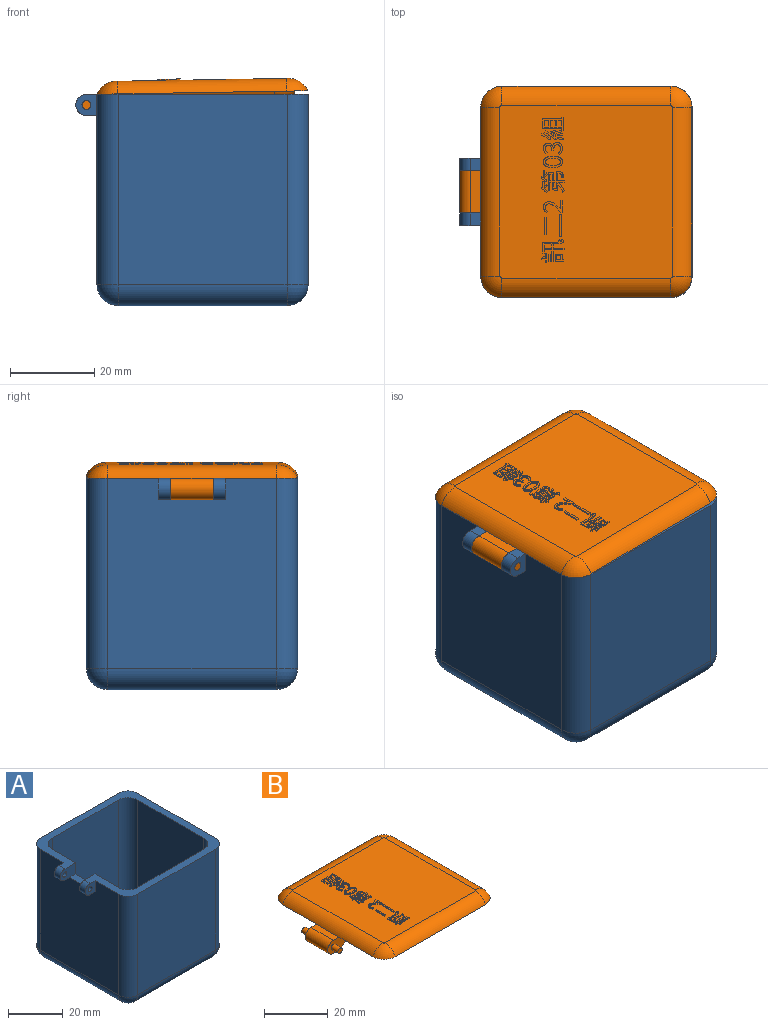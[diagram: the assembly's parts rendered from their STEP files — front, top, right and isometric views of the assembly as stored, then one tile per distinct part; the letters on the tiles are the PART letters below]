
ASSEMBLY  parts=2 mates=1
PART A: 46 faces, bbox 55x50x50 mm
  f0: plane 8x5mm, normal (0,1,0), area 33.9mm2, adj f3,f5,f13,f16,f19,f20
  f1: plane 8x5mm, normal (0,-1,0), area 33.9mm2, adj f3,f4,f13,f16,f18,f21
  f2: plane 5x5mm, normal (0,1,0), area 18.9mm2, adj f3,f4,f6,f18,f21
  f3: plane 52.5x50mm, normal (0,0,1), area 549mm2, adj f0,f1,f2,f6,f7,f8,f9,f11
  f4: plane 3x2.5mm, normal (0,0,-1), area 7.5mm2, adj f1,f2,f6,f18
  f5: plane 3x2.5mm, normal (0,0,-1), area 7.5mm2, adj f0,f6,f17,f19
  f6: plane 45x40mm, normal (-1,0,0), area 1720mm2, adj f2,f3,f4,f5,f16,f17,f34,f36
  f7: plane 45x40mm, normal (1,0,0), area 1800mm2, adj f3,f39,f43,f45
  f8: plane 45x40mm, normal (0,1,0), area 1800mm2, adj f3,f36,f42,f45
  f9: plane 45x40mm, normal (0,-1,0), area 1800mm2, adj f3,f34,f38,f39
  f10: plane 40x40mm, normal (0,0,-1), area 1600mm2, adj f37,f38,f42,f43
  f11: plane 42x34mm, normal (-1,0,0), area 1428mm2, adj f3,f22,f26,f27
  f12: plane 42x34mm, normal (0,-1,0), area 1428mm2, adj f3,f22,f24,f25
  f13: plane 42x34mm, normal (1,0,0), area 1378mm2, adj f0,f1,f3,f16,f24,f30,f33
  f14: plane 42x34mm, normal (0,1,0), area 1428mm2, adj f3,f27,f31,f33
  f15: plane 34x34mm, normal (0,0,1), area 1156mm2, adj f25,f26,f30,f31
  f16: plane 10x3mm, normal (0,0,1), area 30mm2, adj f0,f1,f6,f13
  f17: plane 5x5mm, normal (0,-1,0), area 18.9mm2, adj f3,f5,f6,f19,f20
  f18: cylinder r=2.5mm len=5mm, axis (0,-1,0), area 23.6mm2, adj f1,f2,f3,f4
  f19: cylinder r=2.5mm len=5mm, axis (0,-1,0), area 23.6mm2, adj f0,f3,f5,f17
  f20: cylinder r=1.05mm len=3mm, axis (0,-1,0), area 19.8mm2, adj f0,f17
  f21: cylinder r=1.05mm len=3mm, axis (0,-1,0), area 19.8mm2, adj f1,f2
  f22: cylinder r=5mm len=42mm, axis (0,0,-1), area 329.9mm2, adj f3,f11,f12,f23
  f23: sphere r=5mm, area 39.3mm2, adj f22,f25,f26
  f24: cylinder r=5mm len=42mm, axis (0,0,1), area 329.9mm2, adj f3,f12,f13,f28
  f25: cylinder r=5mm len=34mm, axis (1,0,0), area 267mm2, adj f12,f15,f23,f28
  f26: cylinder r=5mm len=34mm, axis (0,-1,0), area 267mm2, adj f11,f15,f23,f29
  f27: cylinder r=5mm len=42mm, axis (0,0,1), area 329.9mm2, adj f3,f11,f14,f29
  f28: sphere r=5mm, area 39.3mm2, adj f24,f25,f30
  f29: sphere r=5mm, area 39.3mm2, adj f26,f27,f31
  f30: cylinder r=5mm len=34mm, axis (0,1,0), area 267mm2, adj f13,f15,f28,f32
  f31: cylinder r=5mm len=34mm, axis (-1,0,0), area 267mm2, adj f14,f15,f29,f32
  f32: sphere r=5mm, area 39.3mm2, adj f30,f31,f33
  f33: cylinder r=5mm len=42mm, axis (0,0,-1), area 329.9mm2, adj f3,f13,f14,f32
  f34: cylinder r=5mm len=45mm, axis (0,0,1), area 353.4mm2, adj f3,f6,f9,f35
  f35: sphere r=5mm, area 39.3mm2, adj f34,f37,f38
  f36: cylinder r=5mm len=45mm, axis (0,0,-1), area 353.4mm2, adj f3,f6,f8,f40
  f37: cylinder r=5mm len=40mm, axis (0,-1,0), area 314.2mm2, adj f6,f10,f35,f40
  f38: cylinder r=5mm len=40mm, axis (1,0,0), area 314.2mm2, adj f9,f10,f35,f41
  f39: cylinder r=5mm len=45mm, axis (0,0,-1), area 353.4mm2, adj f3,f7,f9,f41
  f40: sphere r=5mm, area 39.3mm2, adj f36,f37,f42
  f41: sphere r=5mm, area 39.3mm2, adj f38,f39,f43
  f42: cylinder r=5mm len=40mm, axis (-1,0,0), area 314.2mm2, adj f8,f10,f40,f44
  f43: cylinder r=5mm len=40mm, axis (0,1,0), area 314.2mm2, adj f7,f10,f41,f44
  f44: sphere r=5mm, area 39.3mm2, adj f42,f43,f45
  f45: cylinder r=5mm len=45mm, axis (0,0,1), area 353.4mm2, adj f3,f7,f8,f44
PART B: 258 faces, bbox 55x50x8.3 mm
  f0: plane 40.84x40.84mm, normal (0,0,1), area 1603.1mm2, adj f12,f13,f14,f15,f17,f18,f19,f20
  f1: plane 12.58x5mm, normal (0,1,0), area 35.6mm2, adj f3,f4,f5,f6,f9,f11,f240,f249
  f2: plane 12.58x5mm, normal (0,-1,0), area 35.6mm2, adj f3,f4,f5,f6,f7,f11,f240,f241
  f3: plane 50x50mm, normal (0,0,-1), area 534mm2, adj f1,f2,f241,f242,f243,f244,f245,f246
  f4: plane 39.42x34.84mm, normal (0,0,-1), area 1259.1mm2, adj f1,f2,f240,f241,f242,f243,f244,f245
  f5: plane 10x1.5mm, normal (0,0,-1), area 15mm2, adj f1,f2,f11,f240
  f6: plane 10x2.5mm, normal (0,0,1), area 25mm2, adj f1,f2,f11,f252
  f7: cylinder r=1mm len=3mm, axis (0,1,0), area 18.8mm2, adj f2,f8
  f8: plane 2x2mm, normal (0,-1,0), area 3.1mm2, adj f7
  f9: cylinder r=1mm len=3mm, axis (0,-1,0), area 18.8mm2, adj f1,f10
  f10: plane 2x2mm, normal (0,1,0), area 3.1mm2, adj f9
  f11: cylinder r=2.5mm len=10mm, axis (0,-1,0), area 78.5mm2, adj f1,f2,f5,f6
  f12: plane 0.33x0.3mm, normal (0.85,0.53,0), area 0.1mm2, adj f0,f13,f15,f16
  f13: extruded ~0.76x0.43mm, area 0.3mm2, adj f0,f12,f14,f16
  f14: plane 0.31x0.3mm, normal (-0.87,-0.49,0), area 0.1mm2, adj f0,f13,f15,f16
  f15: extruded ~0.79x0.42mm, area 0.3mm2, adj f0,f12,f14,f16
  f16: plane 0.97x0.74mm, normal (0,0,1), area 0.3mm2, adj f12,f13,f14,f15
  f17: plane 0.36x0.3mm, normal (0,1,0), area 0.1mm2, adj f0,f18,f20,f21
  f18: plane 2.13x0.3mm, normal (-1,0,0), area 0.6mm2, adj f0,f17,f19,f21
  f19: plane 0.36x0.3mm, normal (0,-1,0), area 0.1mm2, adj f0,f18,f20,f21
  f20: plane 2.13x0.3mm, normal (1,0,0), area 0.6mm2, adj f0,f17,f19,f21
  f21: plane 2.13x0.36mm, normal (0,0,1), area 0.8mm2, adj f17,f18,f19,f20
  f22: plane 1.67x0.3mm, normal (1,0,0), area 0.5mm2, adj f0,f23,f25,f26
  f23: plane 0.35x0.3mm, normal (0,1,0), area 0.1mm2, adj f0,f22,f24,f26
  f24: plane 1.67x0.3mm, normal (-1,0,0), area 0.5mm2, adj f0,f23,f25,f26
  f25: plane 0.35x0.3mm, normal (0,-1,0), area 0.1mm2, adj f0,f22,f24,f26
  f26: plane 1.67x0.35mm, normal (0,0,1), area 0.6mm2, adj f22,f23,f24,f25
  f27: plane 0.96x0.3mm, normal (1,0,0), area 0.3mm2, adj f28,f36,f37,f38
  f28: plane 0.98x0.3mm, normal (0,-1,0), area 0.3mm2, adj f27,f29,f37,f38
  f29: plane 0.96x0.3mm, normal (-1,0,0), area 0.3mm2, adj f28,f36,f37,f38
  f30: plane 1.71x0.3mm, normal (0,1,0), area 0.5mm2, adj f0,f31,f35,f37
  f31: plane 1.68x0.3mm, normal (-1,0,0), area 0.5mm2, adj f0,f30,f32,f37
  f32: plane 1.99x0.3mm, normal (0,-1,0), area 0.6mm2, adj f0,f31,f33,f37
  f33: plane 0.36x0.3mm, normal (1,0,0), area 0.1mm2, adj f0,f32,f34,f37
  f34: plane 0.3x0.28mm, normal (0,1,0), area 0.1mm2, adj f0,f33,f35,f37
  f35: plane 1.32x0.3mm, normal (1,0,0), area 0.4mm2, adj f0,f30,f34,f37
  f36: plane 0.98x0.3mm, normal (0,1,0), area 0.3mm2, adj f27,f29,f37,f38
  f37: plane 1.99x1.68mm, normal (0,0,1), area 2mm2, adj f27,f28,f29,f30,f31,f32,f33,f34
  f38: plane 0.98x0.96mm, normal (0,0,1), area 0.9mm2, adj f27,f28,f29,f36
  f39: plane 0.35x0.3mm, normal (0,-1,0), area 0.1mm2, adj f0,f40,f42,f43
  f40: plane 1.68x0.3mm, normal (1,0,0), area 0.5mm2, adj f0,f39,f41,f43
  f41: plane 0.35x0.3mm, normal (0,1,0), area 0.1mm2, adj f0,f40,f42,f43
  f42: plane 1.68x0.3mm, normal (-1,0,0), area 0.5mm2, adj f0,f39,f41,f43
  f43: plane 1.68x0.35mm, normal (0,0,1), area 0.6mm2, adj f39,f40,f41,f42
  f44: plane 2.58x0.3mm, normal (-1,0,0), area 0.8mm2, adj f0,f45,f63,f64
  f45: plane 0.42x0.3mm, normal (0,-1,0), area 0.1mm2, adj f0,f44,f46,f64
  f46: plane 0.74x0.3mm, normal (1,0,0), area 0.2mm2, adj f0,f45,f47,f64
  f47: plane 1.75x0.3mm, normal (0,-1,0), area 0.5mm2, adj f0,f46,f48,f64
  f48: plane 0.8x0.3mm, normal (-1,0,0), area 0.2mm2, adj f0,f47,f49,f64
  f49: plane 0.41x0.3mm, normal (0,-1,0), area 0.1mm2, adj f0,f48,f50,f64
  f50: plane 0.8x0.3mm, normal (1,0,0), area 0.2mm2, adj f0,f49,f51,f64
  f51: plane 2.5x0.3mm, normal (0,-1,0), area 0.7mm2, adj f0,f50,f52,f64
  f52: plane 0.42x0.3mm, normal (1,0,0), area 0.1mm2, adj f0,f51,f53,f64
  f53: plane 2.5x0.3mm, normal (0,1,0), area 0.7mm2, adj f0,f52,f54,f64
  f54: plane 0.78x0.3mm, normal (1,0,0), area 0.2mm2, adj f0,f53,f55,f64
  f55: plane 0.41x0.3mm, normal (0,1,0), area 0.1mm2, adj f0,f54,f56,f64
  f56: plane 0.78x0.3mm, normal (-1,0,0), area 0.2mm2, adj f0,f55,f57,f64
  f57: plane 1.75x0.3mm, normal (0,1,0), area 0.5mm2, adj f0,f56,f58,f64
  f58: plane 0.98x0.3mm, normal (1,0,0), area 0.3mm2, adj f0,f57,f59,f64
  f59: extruded ~4.55x0.56mm, area 1.4mm2, adj f0,f58,f60,f64
  f60: extruded ~0.94x0.53mm, area 0.4mm2, adj f0,f59,f61,f64
  f61: extruded ~0.32x0.3mm, area 0.1mm2, adj f0,f60,f62,f64
  f62: extruded ~0.8x0.3mm, area 0.2mm2, adj f0,f61,f63,f64
  f63: extruded ~4.54x0.3mm, area 1.4mm2, adj f0,f44,f62,f64
  f64: plane 5.08x3.29mm, normal (0,0,1), area 5.9mm2, adj f44,f45,f46,f47,f48,f49,f50,f51
  f65: plane 4.23x0.3mm, normal (-1,0,0), area 1.3mm2, adj f0,f66,f68,f69
  f66: plane 0.47x0.3mm, normal (0,-1,0), area 0.1mm2, adj f0,f65,f67,f69
  f67: plane 4.23x0.3mm, normal (1,0,0), area 1.3mm2, adj f0,f66,f68,f69
  f68: plane 0.47x0.3mm, normal (0,1,0), area 0.1mm2, adj f0,f65,f67,f69
  f69: plane 4.23x0.47mm, normal (0,0,1), area 2mm2, adj f65,f66,f67,f68
  f70: plane 5.23x0.3mm, normal (-1,0,0), area 1.6mm2, adj f0,f71,f73,f74
  f71: plane 0.48x0.3mm, normal (0,-1,0), area 0.1mm2, adj f0,f70,f72,f74
  f72: plane 5.23x0.3mm, normal (1,0,0), area 1.6mm2, adj f0,f71,f73,f74
  f73: plane 0.48x0.3mm, normal (0,1,0), area 0.1mm2, adj f0,f70,f72,f74
  f74: plane 5.23x0.48mm, normal (0,0,1), area 2.5mm2, adj f70,f71,f72,f73
  f75: plane 0.32x0.3mm, normal (0,-1,0), area 0.1mm2, adj f0,f76,f86,f87
  f76: plane 2.73x0.3mm, normal (1,0,0), area 0.8mm2, adj f0,f75,f77,f87
  f77: plane 0.47x0.3mm, normal (0,1,0), area 0.1mm2, adj f0,f76,f78,f87
  f78: plane 1.2x0.3mm, normal (-1,0,0), area 0.4mm2, adj f0,f77,f79,f87
  f79: extruded ~0.71x0.3mm, area 0.2mm2, adj f0,f78,f80,f87
  f80: extruded ~2.72x1.7mm, area 1mm2, adj f0,f79,f81,f87
  f81: extruded ~1.29x1.26mm, area 0.6mm2, adj f0,f80,f82,f87
  f82: extruded ~1.28x0.64mm, area 0.4mm2, adj f0,f81,f83,f87
  f83: plane 0.31x0.31mm, normal (0.71,-0.7,0), area 0.1mm2, adj f0,f82,f84,f87
  f84: extruded ~0.9x0.5mm, area 0.3mm2, adj f0,f83,f85,f87
  f85: extruded ~0.86x0.8mm, area 0.4mm2, adj f0,f84,f86,f87
  f86: extruded ~2.81x1.99mm, area 1.1mm2, adj f0,f75,f85,f87
  f87: plane 4.43x2.76mm, normal (0,0,1), area 4.3mm2, adj f75,f76,f77,f78,f79,f80,f81,f82
  f88: plane 0.51x0.3mm, normal (1,0,0), area 0.2mm2, adj f0,f89,f100,f101
  f89: plane 0.3x0.23mm, normal (-0.8,-0.61,0), area 0.1mm2, adj f0,f88,f90,f101
  f90: extruded ~0.6x0.56mm, area 0.2mm2, adj f0,f89,f91,f101
  f91: plane 0.3x0.29mm, normal (0.77,0.64,0), area 0.1mm2, adj f0,f90,f92,f101
  f92: extruded ~0.53x0.53mm, area 0.2mm2, adj f0,f91,f93,f101
  f93: plane 1.12x0.3mm, normal (1,0,0), area 0.3mm2, adj f0,f92,f94,f101
  f94: plane 0.36x0.3mm, normal (0,1,0), area 0.1mm2, adj f0,f93,f95,f101
  f95: plane 1.52x0.3mm, normal (-1,0,0), area 0.5mm2, adj f0,f94,f96,f101
  f96: extruded ~0.36x0.3mm, area 0.1mm2, adj f0,f95,f97,f101
  f97: plane 0.39x0.3mm, normal (-0.96,0.27,0), area 0.1mm2, adj f0,f96,f98,f101
  f98: extruded ~1.29x0.9mm, area 0.5mm2, adj f0,f97,f99,f101
  f99: extruded ~0.31x0.3mm, area 0.1mm2, adj f0,f98,f100,f101
  f100: extruded ~0.77x0.61mm, area 0.3mm2, adj f0,f88,f99,f101
  f101: plane 2.64x1.6mm, normal (0,0,1), area 1.5mm2, adj f88,f89,f90,f91,f92,f93,f94,f95
  f102: plane 1.33x0.3mm, normal (1,0,0), area 0.4mm2, adj f103,f135,f136,f138
  f103: plane 0.55x0.3mm, normal (0,-1,0), area 0.2mm2, adj f102,f104,f136,f138
  f104: plane 1.42x0.3mm, normal (-1,0,0), area 0.4mm2, adj f103,f135,f136,f138
  f105: plane 0.55x0.3mm, normal (0,1,0), area 0.2mm2, adj f106,f133,f136,f137
  f106: plane 1.55x0.3mm, normal (1,0,0), area 0.5mm2, adj f105,f107,f136,f137
  f107: plane 0.55x0.3mm, normal (0,-1,0), area 0.2mm2, adj f106,f133,f136,f137
  f108: plane 2.18x0.3mm, normal (-1,0,0), area 0.7mm2, adj f0,f109,f134,f136
  f109: plane 0.55x0.3mm, normal (0,1,0), area 0.2mm2, adj f0,f108,f110,f136
  f110: plane 1.99x0.3mm, normal (1,0,0), area 0.6mm2, adj f0,f109,f111,f136
  f111: plane 1.29x0.3mm, normal (0,1,0), area 0.4mm2, adj f0,f110,f112,f136
  f112: plane 4.34x0.3mm, normal (-1,0,0), area 1.3mm2, adj f0,f111,f113,f136
  f113: plane 0.37x0.3mm, normal (0,-1,0), area 0.1mm2, adj f0,f112,f114,f136
  f114: plane 1.92x0.3mm, normal (1,0,0), area 0.6mm2, adj f0,f113,f115,f136
  f115: plane 0.55x0.3mm, normal (0,-1,0), area 0.2mm2, adj f0,f114,f116,f136
  f116: plane 1.71x0.3mm, normal (-1,0,0), area 0.5mm2, adj f0,f115,f117,f136
  f117: extruded ~1.31x0.3mm, area 0.4mm2, adj f0,f116,f118,f136
  f118: plane 1.57x0.3mm, normal (1,0,0), area 0.5mm2, adj f0,f117,f119,f136
  f119: extruded ~1.93x1.19mm, area 0.7mm2, adj f0,f118,f120,f136
  f120: extruded ~0.35x0.3mm, area 0.1mm2, adj f0,f119,f121,f136
  f121: extruded ~1.99x1.37mm, area 0.7mm2, adj f0,f120,f122,f136
  f122: plane 1.36x0.3mm, normal (0,-1,0), area 0.4mm2, adj f0,f121,f123,f136
  f123: plane 0.43x0.3mm, normal (1,0,0), area 0.1mm2, adj f0,f122,f124,f136
  f124: plane 1.53x0.3mm, normal (0,1,0), area 0.5mm2, adj f0,f123,f125,f136
  f125: plane 1.71x0.3mm, normal (1,0,0), area 0.5mm2, adj f0,f124,f126,f136
  f126: extruded ~0.85x0.3mm, area 0.3mm2, adj f0,f125,f127,f136
  f127: extruded ~0.3x0.21mm, area 0.1mm2, adj f0,f126,f128,f136
  f128: extruded ~0.67x0.3mm, area 0.2mm2, adj f0,f127,f129,f136
  f129: extruded ~0.41x0.3mm, area 0.1mm2, adj f0,f128,f130,f136
  f130: extruded ~0.75x0.3mm, area 0.2mm2, adj f0,f129,f131,f136
  f131: extruded ~0.37x0.3mm, area 0.1mm2, adj f0,f130,f132,f136
  f132: extruded ~1.32x0.31mm, area 0.4mm2, adj f0,f131,f134,f136
  f133: plane 1.55x0.3mm, normal (-1,0,0), area 0.5mm2, adj f105,f107,f136,f137
  f134: extruded ~0.3x0.18mm, area 0.1mm2, adj f0,f108,f132,f136
  f135: extruded ~0.55x0.3mm, area 0.2mm2, adj f102,f104,f136,f138
  f136: plane 4.89x3.76mm, normal (0,0,1), area 8.3mm2, adj f102,f103,f104,f105,f106,f107,f108,f109
  f137: plane 1.55x0.55mm, normal (0,0,1), area 0.8mm2, adj f105,f106,f107,f133
  f138: plane 1.42x0.55mm, normal (0,0,1), area 0.8mm2, adj f102,f103,f104,f135
  f139: plane 1.79x0.3mm, normal (-1,0,0), area 0.5mm2, adj f0,f140,f151,f152
  f140: extruded ~0.37x0.3mm, area 0.1mm2, adj f0,f139,f141,f152
  f141: plane 0.41x0.3mm, normal (-0.97,0.23,0), area 0.1mm2, adj f0,f140,f142,f152
  f142: extruded ~1.1x0.74mm, area 0.4mm2, adj f0,f141,f143,f152
  f143: extruded ~0.33x0.3mm, area 0.1mm2, adj f0,f142,f144,f152
  f144: extruded ~0.55x0.45mm, area 0.2mm2, adj f0,f143,f145,f152
  f145: plane 0.66x0.3mm, normal (1,0,0), area 0.2mm2, adj f0,f144,f146,f152
  f146: plane 0.3x0.26mm, normal (-0.78,-0.63,0), area 0.1mm2, adj f0,f145,f147,f152
  f147: extruded ~0.61x0.58mm, area 0.3mm2, adj f0,f146,f148,f152
  f148: plane 0.3x0.29mm, normal (0.76,0.65,0), area 0.1mm2, adj f0,f147,f149,f152
  f149: extruded ~0.59x0.53mm, area 0.2mm2, adj f0,f148,f150,f152
  f150: plane 1.28x0.3mm, normal (1,0,0), area 0.4mm2, adj f0,f149,f151,f152
  f151: plane 0.35x0.3mm, normal (0,1,0), area 0.1mm2, adj f0,f139,f150,f152
  f152: plane 2.78x1.6mm, normal (0,0,1), area 1.6mm2, adj f139,f140,f141,f142,f143,f144,f145,f146
  f153: extruded ~2.27x1.36mm, area 0.9mm2, adj f0,f154,f160,f161
  f154: extruded ~2.27x1.35mm, area 0.9mm2, adj f0,f153,f155,f161
  f155: extruded ~2.24x1.35mm, area 0.9mm2, adj f0,f154,f160,f161
  f156: extruded ~1.83x0.83mm, area 0.7mm2, adj f157,f159,f161,f162
  f157: extruded ~1.83x0.83mm, area 0.7mm2, adj f156,f158,f161,f162
  f158: extruded ~1.8x0.83mm, area 0.7mm2, adj f157,f159,f161,f162
  f159: extruded ~1.8x0.83mm, area 0.7mm2, adj f156,f158,f161,f162
  f160: extruded ~2.24x1.36mm, area 0.9mm2, adj f0,f153,f155,f161
  f161: plane 4.51x2.71mm, normal (0,0,1), area 5.1mm2, adj f153,f154,f155,f156,f157,f158,f159,f160
  f162: plane 3.64x1.66mm, normal (0,0,1), area 5mm2, adj f156,f157,f158,f159
  f163: extruded ~1.39x0.59mm, area 0.5mm2, adj f0,f164,f178,f179
  f164: extruded ~1.39x1.24mm, area 0.6mm2, adj f0,f163,f165,f179
  f165: extruded ~1.1x0.93mm, area 0.5mm2, adj f0,f164,f166,f179
  f166: plane 0.3x0.02mm, normal (0,1,0), area 0mm2, adj f0,f165,f167,f179
  f167: extruded ~1.05x0.78mm, area 0.4mm2, adj f0,f166,f168,f179
  f168: extruded ~1.26x1.09mm, area 0.6mm2, adj f0,f167,f169,f179
  f169: extruded ~1.22x0.52mm, area 0.4mm2, adj f0,f168,f170,f179
  f170: plane 0.35x0.3mm, normal (0.65,-0.76,0), area 0.1mm2, adj f0,f169,f171,f179
  f171: extruded ~0.9x0.43mm, area 0.3mm2, adj f0,f170,f172,f179
  f172: extruded ~0.74x0.7mm, area 0.3mm2, adj f0,f171,f173,f179
  f173: extruded ~1.2x0.83mm, area 0.5mm2, adj f0,f172,f174,f179
  f174: plane 0.42x0.3mm, normal (0,-1,0), area 0.1mm2, adj f0,f173,f175,f179
  f175: extruded ~1.35x0.87mm, area 0.5mm2, adj f0,f174,f176,f179
  f176: extruded ~0.88x0.81mm, area 0.4mm2, adj f0,f175,f177,f179
  f177: extruded ~1.08x0.5mm, area 0.4mm2, adj f0,f176,f178,f179
  f178: plane 0.36x0.3mm, normal (-0.61,-0.79,0), area 0.1mm2, adj f0,f163,f177,f179
  f179: plane 4.51x2.79mm, normal (0,0,1), area 4.4mm2, adj f163,f164,f165,f166,f167,f168,f169,f170
  f180: plane 0.37x0.3mm, normal (0.95,0.31,0), area 0.1mm2, adj f0,f181,f199,f200
  f181: extruded ~1.23x0.4mm, area 0.4mm2, adj f0,f180,f182,f200
  f182: plane 0.34x0.3mm, normal (-0.96,-0.28,0), area 0.1mm2, adj f0,f181,f183,f200
  f183: extruded ~0.55x0.3mm, area 0.2mm2, adj f0,f182,f184,f200
  f184: plane 1.05x0.3mm, normal (-0.99,-0.13,0), area 0.3mm2, adj f0,f183,f185,f200
  f185: extruded ~1.89x1.41mm, area 0.7mm2, adj f0,f184,f186,f200
  f186: plane 0.38x0.3mm, normal (-0.85,0.52,0), area 0.1mm2, adj f0,f185,f187,f200
  f187: extruded ~0.78x0.46mm, area 0.3mm2, adj f0,f186,f188,f200
  f188: plane 0.69x0.3mm, normal (-1,-0.09,0), area 0.2mm2, adj f0,f187,f189,f200
  f189: extruded ~1.58x0.97mm, area 0.6mm2, adj f0,f188,f190,f200
  f190: plane 0.4x0.3mm, normal (-0.92,0.39,0), area 0.1mm2, adj f0,f189,f191,f200
  f191: extruded ~1.5x0.83mm, area 0.5mm2, adj f0,f190,f192,f200
  f192: extruded ~0.34x0.33mm, area 0.1mm2, adj f0,f191,f193,f200
  f193: extruded ~0.4x0.3mm, area 0.1mm2, adj f0,f192,f194,f200
  f194: extruded ~0.9x0.3mm, area 0.3mm2, adj f0,f193,f195,f200
  f195: extruded ~0.68x0.54mm, area 0.3mm2, adj f0,f194,f196,f200
  f196: extruded ~0.45x0.39mm, area 0.2mm2, adj f0,f195,f197,f200
  f197: extruded ~0.42x0.3mm, area 0.1mm2, adj f0,f196,f198,f200
  f198: extruded ~1.71x0.32mm, area 0.5mm2, adj f0,f197,f199,f200
  f199: extruded ~0.36x0.3mm, area 0.1mm2, adj f0,f180,f198,f200
  f200: plane 3.59x2.33mm, normal (0,0,1), area 3.4mm2, adj f180,f181,f182,f183,f184,f185,f186,f187
  f201: plane 0.37x0.3mm, normal (-0.99,0.16,0), area 0.1mm2, adj f0,f202,f204,f205
  f202: extruded ~1.36x0.3mm, area 0.4mm2, adj f0,f201,f203,f205
  f203: extruded ~0.36x0.3mm, area 0.1mm2, adj f0,f202,f204,f205
  f204: extruded ~1.44x0.3mm, area 0.4mm2, adj f0,f201,f203,f205
  f205: plane 1.5x0.66mm, normal (0,0,1), area 0.5mm2, adj f201,f202,f203,f204
  f206: plane 0.35x0.3mm, normal (-0.98,-0.18,0), area 0.1mm2, adj f0,f207,f209,f210
  f207: extruded ~1.28x0.3mm, area 0.4mm2, adj f0,f206,f208,f210
  f208: plane 0.37x0.3mm, normal (0.98,0.19,0), area 0.1mm2, adj f0,f207,f209,f210
  f209: extruded ~1.27x0.3mm, area 0.4mm2, adj f0,f206,f208,f210
  f210: plane 1.34x0.52mm, normal (0,0,1), area 0.5mm2, adj f206,f207,f208,f209
  f211: plane 0.33x0.3mm, normal (-0.95,-0.31,0), area 0.1mm2, adj f0,f212,f214,f215
  f212: extruded ~1.02x0.3mm, area 0.3mm2, adj f0,f211,f213,f215
  f213: plane 0.35x0.3mm, normal (0.95,0.32,0), area 0.1mm2, adj f0,f212,f214,f215
  f214: extruded ~1.01x0.31mm, area 0.3mm2, adj f0,f211,f213,f215
  f215: plane 1.13x0.64mm, normal (0,0,1), area 0.4mm2, adj f211,f212,f213,f214
  f216: plane 1.16x0.3mm, normal (0,1,0), area 0.3mm2, adj f217,f235,f236,f239
  f217: plane 1.53x0.3mm, normal (1,0,0), area 0.5mm2, adj f216,f218,f236,f239
  f218: plane 1.16x0.3mm, normal (0,-1,0), area 0.3mm2, adj f217,f235,f236,f239
  f219: plane 1.53x0.3mm, normal (1,0,0), area 0.5mm2, adj f220,f232,f236,f238
  f220: plane 1.1x0.3mm, normal (0,-1,0), area 0.3mm2, adj f219,f221,f236,f238
  f221: plane 1.53x0.3mm, normal (-1,0,0), area 0.5mm2, adj f220,f232,f236,f238
  f222: plane 1.13x0.3mm, normal (0,-1,0), area 0.3mm2, adj f223,f233,f236,f237
  f223: plane 1.53x0.3mm, normal (-1,0,0), area 0.5mm2, adj f222,f224,f236,f237
  f224: plane 1.13x0.3mm, normal (0,1,0), area 0.3mm2, adj f223,f233,f236,f237
  f225: plane 0.4x0.3mm, normal (-1,0,0), area 0.1mm2, adj f0,f226,f234,f236
  f226: plane 4.59x0.3mm, normal (0,1,0), area 1.4mm2, adj f0,f225,f227,f236
  f227: plane 2.36x0.3mm, normal (-1,0,0), area 0.7mm2, adj f0,f226,f228,f236
  f228: plane 4.59x0.3mm, normal (0,-1,0), area 1.4mm2, adj f0,f227,f229,f236
  f229: plane 0.52x0.3mm, normal (-1,0,0), area 0.2mm2, adj f0,f228,f230,f236
  f230: plane 0.4x0.3mm, normal (0,-1,0), area 0.1mm2, adj f0,f229,f231,f236
  f231: plane 3.28x0.3mm, normal (1,0,0), area 1mm2, adj f0,f230,f234,f236
  f232: plane 1.1x0.3mm, normal (0,1,0), area 0.3mm2, adj f219,f221,f236,f238
  f233: plane 1.53x0.3mm, normal (1,0,0), area 0.5mm2, adj f222,f224,f236,f237
  f234: plane 0.4x0.3mm, normal (0,1,0), area 0.1mm2, adj f0,f225,f231,f236
  f235: plane 1.53x0.3mm, normal (-1,0,0), area 0.5mm2, adj f216,f218,f236,f239
  f236: plane 4.99x3.28mm, normal (0,0,1), area 7mm2, adj f216,f217,f218,f219,f220,f221,f222,f223
  f237: plane 1.53x1.13mm, normal (0,0,1), area 1.7mm2, adj f222,f223,f224,f233
  f238: plane 1.53x1.1mm, normal (0,0,1), area 1.7mm2, adj f219,f220,f221,f232
  f239: plane 1.53x1.16mm, normal (0,0,1), area 1.8mm2, adj f216,f217,f218,f235
  f240: cylinder r=5mm len=10mm, axis (0,-1,0), area 46.4mm2, adj f1,f2,f4,f5
  f241: cylinder r=5mm len=12mm, axis (0,1,0), area 69.6mm2, adj f2,f3,f4,f242
  f242: torus R=0.42mm, axis (0,0,1), area 27.4mm2, adj f3,f4,f241,f243
  f243: cylinder r=5mm len=34mm, axis (-1,0,0), area 197.1mm2, adj f3,f4,f242,f244
  f244: torus R=0.42mm, axis (0,0,1), area 27.4mm2, adj f3,f4,f243,f245
  f245: cylinder r=5mm len=34mm, axis (0,1,0), area 197.1mm2, adj f3,f4,f244,f246
  f246: torus R=0.42mm, axis (0,0,1), area 27.4mm2, adj f3,f4,f245,f247
  f247: cylinder r=5mm len=34mm, axis (-1,0,0), area 197.1mm2, adj f3,f4,f246,f248
  f248: torus R=0.42mm, axis (0,0,1), area 27.4mm2, adj f3,f4,f247,f249
  f249: cylinder r=5mm len=12mm, axis (0,1,0), area 69.6mm2, adj f1,f3,f4,f248
  f250: torus R=0.42mm, axis (0,0,-1), area 27.4mm2, adj f0,f3,f251,f252
  f251: cylinder r=5mm len=40mm, axis (1,0,0), area 231.9mm2, adj f0,f3,f250,f253
  f252: cylinder r=5mm len=40mm, axis (0,-1,0), area 231.9mm2, adj f0,f3,f6,f250,f254
  f253: torus R=0.42mm, axis (0,0,-1), area 27.4mm2, adj f0,f3,f251,f255
  f254: torus R=0.42mm, axis (0,0,-1), area 27.4mm2, adj f0,f3,f252,f256
  f255: cylinder r=5mm len=40mm, axis (0,-1,0), area 231.9mm2, adj f0,f3,f253,f257
  f256: cylinder r=5mm len=40mm, axis (1,0,0), area 231.9mm2, adj f0,f3,f254,f257
  f257: torus R=0.42mm, axis (0,0,-1), area 27.4mm2, adj f0,f3,f255,f256
PLACE A t=(-5.86,9.94,-2.37)mm fixed
PLACE B rot(axis=(0,-1,0),0.9deg) t=(-5.9,9.94,48.09)mm
MATE revolute B.f7 <-> A.f18  axis (0,-1,0) through (-33.36,1.94,45.13)mm
